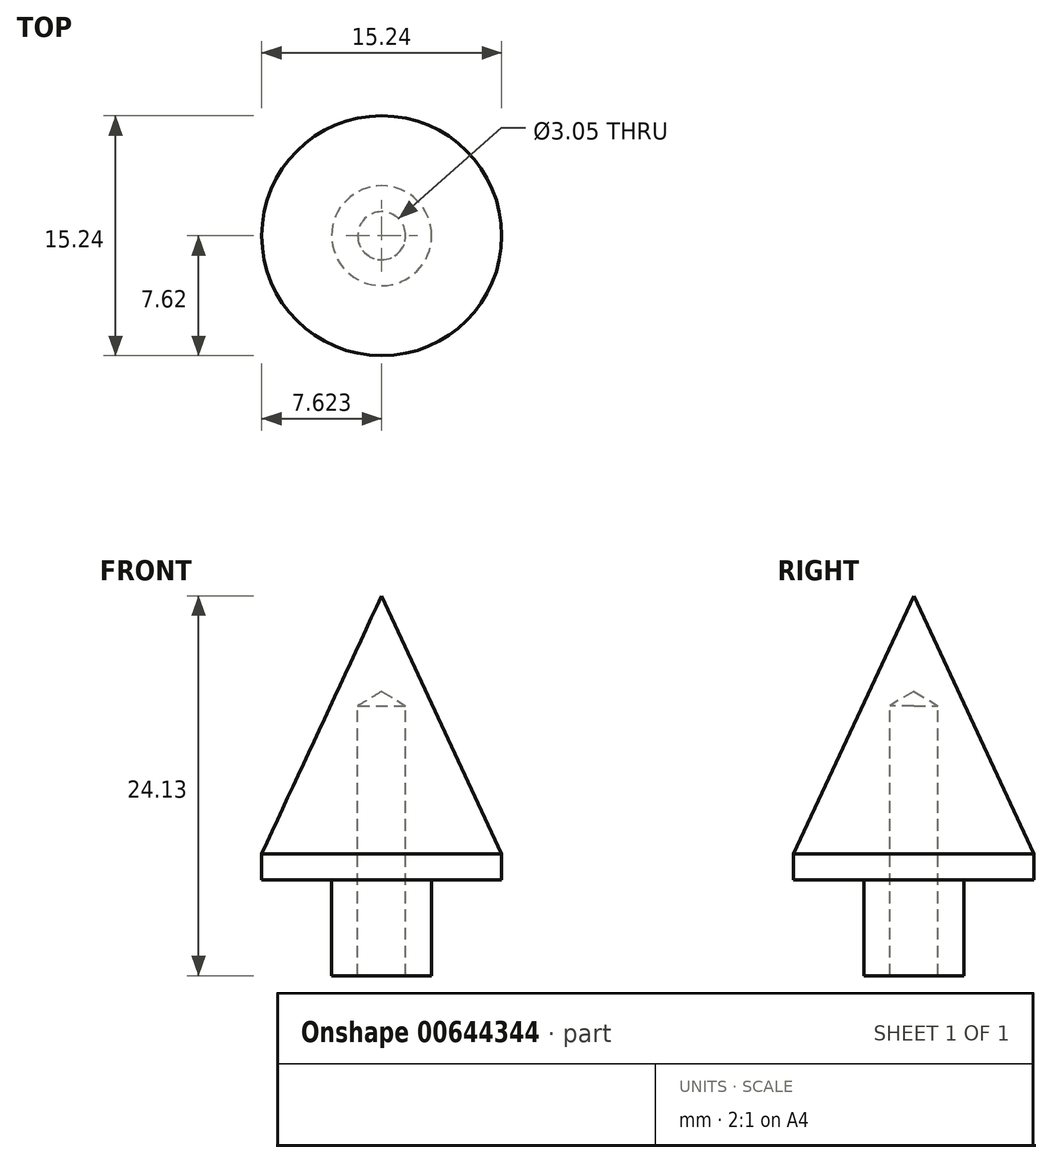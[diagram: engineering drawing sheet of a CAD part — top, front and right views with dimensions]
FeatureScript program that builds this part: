
annotation { "Feature Type Name" : "Feature", "Feature Type Description" : "" }
export const myFeature = defineFeature(function(context is Context, id is Id, definition is map)
    precondition{}
    {
        {
            var Q0;
            Q0=qCreatedBy(makeId("Front.planeOp"),FACE);
            var sketch = newSketch(context, id + "F0", { "sketchPlane" : qUnion([Q0])});
            skLineSegment(sketch, "E0", {"start": v(-11.96, 16.38) * mm, "end": v(-11.96, -1.65) * mm});
            skLineSegment(sketch, "E1", {"start": v(-11.96, 16.38) * mm, "end": v(-19.58, 0) * mm});
            skLineSegment(sketch, "E2", {"start": v(-19.58, 0) * mm, "end": v(-19.58, -1.65) * mm});
            skLineSegment(sketch, "E3", {"start": v(-11.96, -1.65) * mm, "end": v(-19.58, -1.65) * mm});
            skLineSegment(sketch, "E4", {"start": v(-15.13, -1.65) * mm, "end": v(-15.13, -7.75) * mm});
            skLineSegment(sketch, "E5", {"start": v(-15.13, -7.75) * mm, "end": v(-11.96, -7.75) * mm});
            skLineSegment(sketch, "E6", {"start": v(-11.96, -7.75) * mm, "end": v(-11.96, -1.65) * mm});
            skSolve(sketch);
        }
        {
            var Q0;
            {var subQ1=sQuery(id+"F0.wireOp",EDGE,"E0");Q0=makeQuery(id+"F0.imprint","IMPRINT",FACE,{"disambiguationData":[TD([[makeQuery(id+"F0.imprint","IMPRINT",EDGE,{"derivedFrom":subQ1}),-1.0]])]});}
            var Q1;
            {var subQ2=sQuery(id+"F0.wireOp",EDGE,"E4");Q1=makeQuery(id+"F0.imprint","IMPRINT",FACE,{"disambiguationData":[TD([[makeQuery(id+"F0.imprint","IMPRINT",EDGE,{"derivedFrom":subQ2}),1.0]])]});}
            var Q2;
            Q2=sQuery(id+"F0.wireOp",EDGE,"E0");
            revolve(context, id + "F1", {"entities" : qUnion([Q0, Q1]), "axis" : qUnion([Q2]), "revolveType" : RevolveType.FULL});
        }
        {
            var Q0;
            Q0=makeQuery(id+"F1.opRevolve","SWEPT_FACE",FACE,{"disambiguationData":[OSD([sQuery(id+"F0.wireOp",EDGE,"E5")])]});
            var sketch = newSketch(context, id + "F2", { "sketchPlane" : qUnion([Q0])});
            skCircle(sketch, "E7", {"center": v(-11.96, 0) * mm, "radius": 1.1 * mm});
            skSolve(sketch);
        }
        {
            var Q0;
            Q0=sQuery(id+"F2.wireOp",VERTEX,"E7.center");
            var Q1;
            Q1=makeQuery(id+"F1.opRevolve","SWEPT_BODY",BODY,{"disambiguationData":[OSD([sQuery(id+"F0.wireOp",EDGE,"E0"),sQuery(id+"F0.wireOp",EDGE,"E1"),sQuery(id+"F0.wireOp",EDGE,"E2"),sQuery(id+"F0.wireOp",EDGE,"E3"),sQuery(id+"F0.wireOp",EDGE,"E4"),sQuery(id+"F0.wireOp",EDGE,"E5"),sQuery(id+"F0.wireOp",EDGE,"E6")])]});
            hole(context, id + "F3", {"style" : HoleStyle.SIMPLE, "endStyle" : HoleEndStyle.BLIND, "holeDiameter" : 3.05 * mm, "majorDiameter" : 6.35 * mm, "holeDepth" : 17.14 * mm, "isTappedThrough" : true, "tappedDepth" : 12.7 * mm, "tapClearance" : 3, "locations" : qUnion([Q0]), "scope" : qUnion([Q1])});
        }
    });
